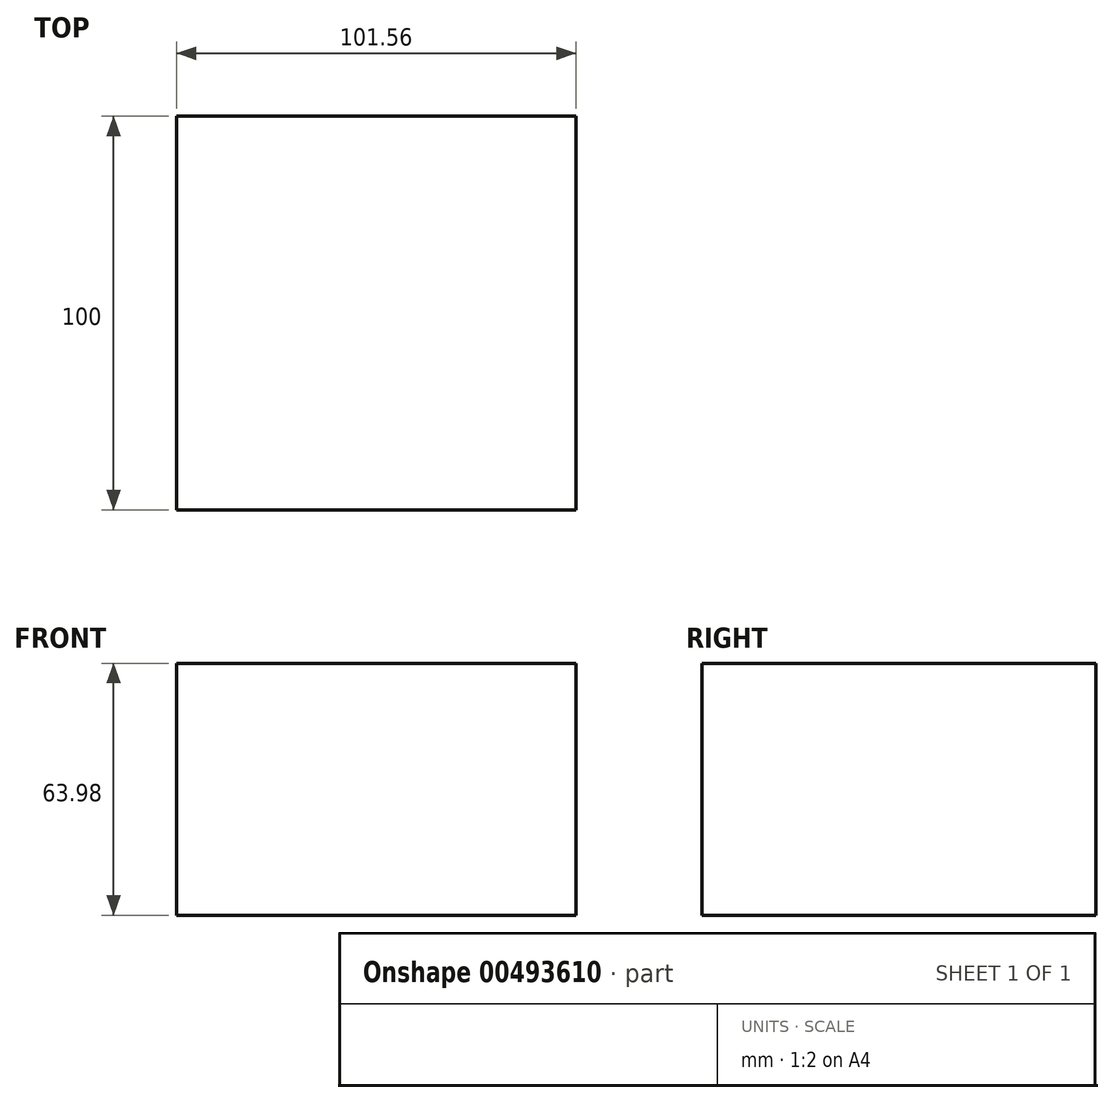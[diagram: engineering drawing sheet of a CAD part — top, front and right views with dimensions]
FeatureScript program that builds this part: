
annotation { "Feature Type Name" : "Feature", "Feature Type Description" : "" }
export const myFeature = defineFeature(function(context is Context, id is Id, definition is map)
    precondition{}
    {
        {
            var Q0;
            Q0=qCreatedBy(makeId("Front.planeOp"),FACE);
            var sketch = newSketch(context, id + "F0", { "sketchPlane" : qUnion([Q0])});
            skLineSegment(sketch, "E0.bottom", {"start": v(-50.78, 31.99) * mm, "end": v(50.78, 31.99) * mm});
            skLineSegment(sketch, "E0.top", {"start": v(-50.78, -31.99) * mm, "end": v(50.78, -31.99) * mm});
            skLineSegment(sketch, "E0.left", {"start": v(-50.78, 31.99) * mm, "end": v(-50.78, -31.99) * mm});
            skLineSegment(sketch, "E0.right", {"start": v(50.78, 31.99) * mm, "end": v(50.78, -31.99) * mm});
            skPoint(sketch, "E0.middle", {"position": v(0, 0) * mm});
            skSolve(sketch);
        }
        {
            var Q0;
            Q0=makeQuery(id+"F0.imprint","IMPRINT",FACE,{"disambiguationData":[TD([[makeQuery(id+"F0.imprint","IMPRINT",EDGE,{"derivedFrom":sQuery(id+"F0.wireOp",EDGE,"E0.bottom")}),-1.0]])]});
            extrude(context, id + "F1", {"entities" : qUnion([Q0]), "depth" : 100 * mm});
        }
    });
